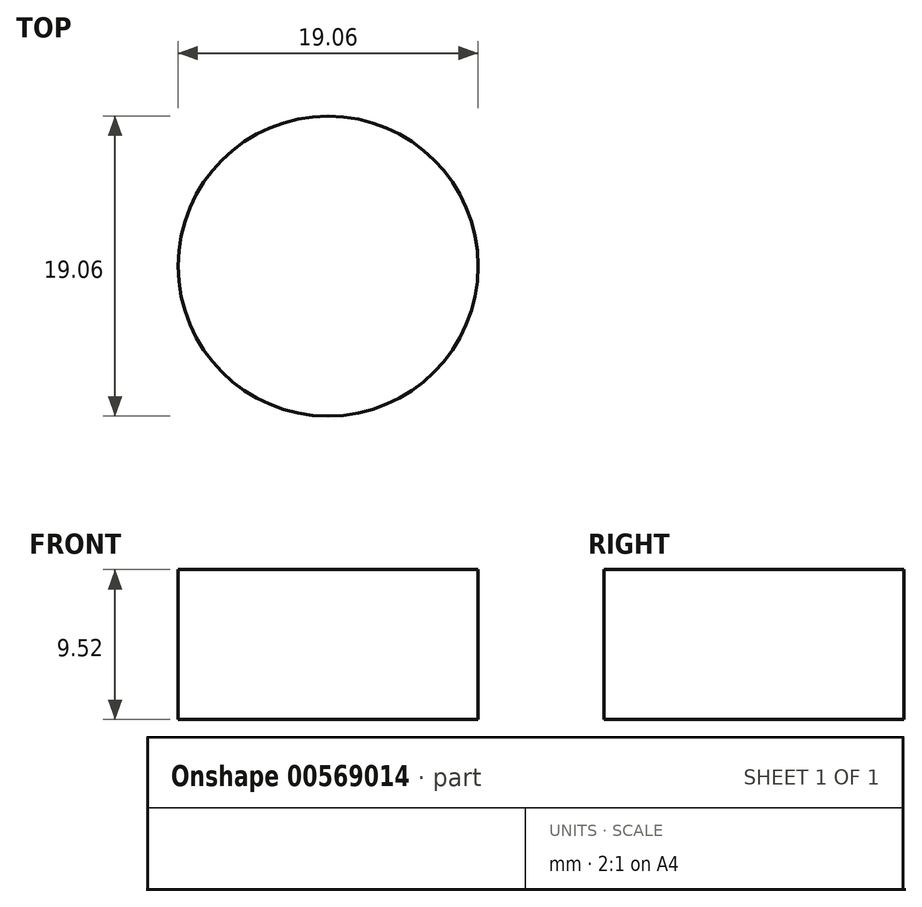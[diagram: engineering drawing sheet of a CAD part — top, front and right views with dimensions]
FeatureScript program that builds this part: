
annotation { "Feature Type Name" : "Feature", "Feature Type Description" : "" }
export const myFeature = defineFeature(function(context is Context, id is Id, definition is map)
    precondition{}
    {
        {
            var Q0;
            Q0=qCreatedBy(makeId("Top.planeOp"),FACE);
            var sketch = newSketch(context, id + "F0", { "sketchPlane" : qUnion([Q0])});
            skCircle(sketch, "E0", {"center": v(0, 0) * mm, "radius": 9.53 * mm});
            skSolve(sketch);
        }
        {
            var Q0;
            Q0 = qSketchRegion(id + "F0", true);
            extrude(context, id + "F1", {"entities" : qUnion([Q0]), "endBound" : BoundingType.SYMMETRIC, "depth" : 9.52 * mm, "offsetDistance" : 25.4 * mm});
        }
    });
